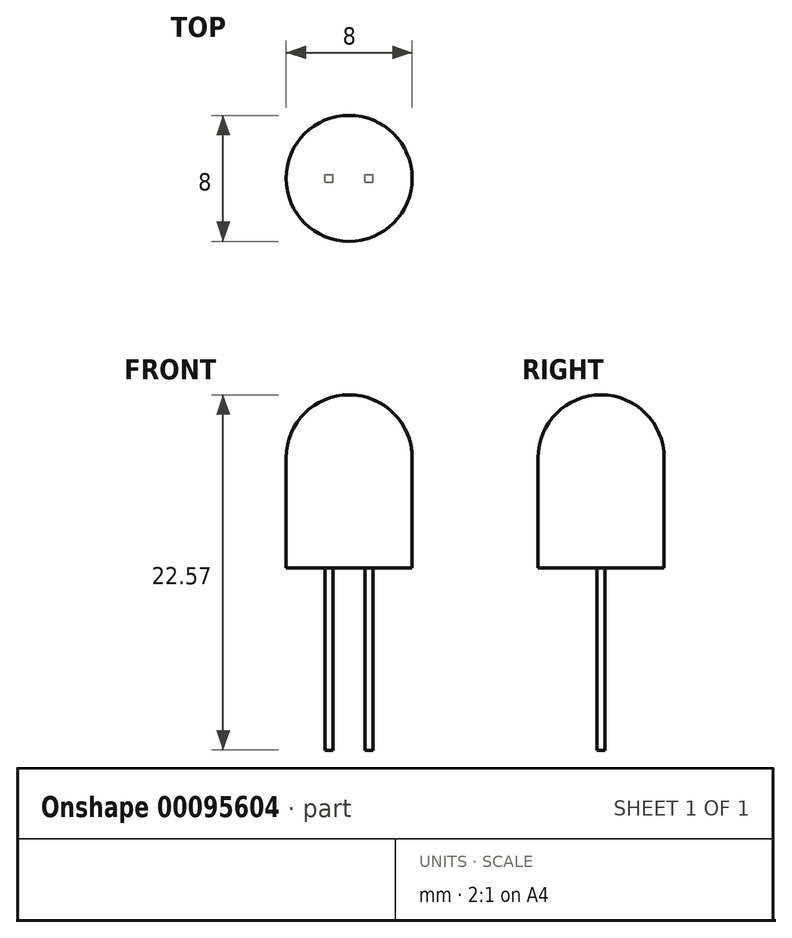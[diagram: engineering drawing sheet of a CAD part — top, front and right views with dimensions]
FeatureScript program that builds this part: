
annotation { "Feature Type Name" : "Feature", "Feature Type Description" : "" }
export const myFeature = defineFeature(function(context is Context, id is Id, definition is map)
    precondition{}
    {
        {
            var Q0;
            Q0=qCreatedBy(makeId("Front.planeOp"),FACE);
            var sketch = newSketch(context, id + "F0", { "sketchPlane" : qUnion([Q0])});
            skLineSegment(sketch, "E0", {"start": v(0, 0) * mm, "end": v(0, 11) * mm});
            skLineSegment(sketch, "E1", {"start": v(0, 0) * mm, "end": v(4, 0) * mm});
            skLineSegment(sketch, "E2", {"start": v(4, 0) * mm, "end": v(4, 7) * mm});
            skArc(sketch, "E3", {"start": v(4, 7) * mm, "mid": v(2.83, 9.83) * mm, "end": v(0, 11) * mm});
            skLineSegment(sketch, "E4", {"start": v(0, 0) * mm, "end": v(0, -3.6) * mm, "construction": true});
            skSolve(sketch);
        }
        {
            var Q0;
            Q0 = qSketchRegion(id + "F0", true);
            var Q1;
            Q1=sQuery(id+"F0.wireOp",EDGE,"E4");
            revolve(context, id + "F1", {"entities" : qUnion([Q0]), "axis" : qUnion([Q1]), "revolveType" : RevolveType.FULL});
        }
        {
            var Q0;
            Q0=qCreatedBy(makeId("Front.planeOp"),FACE);
            var sketch = newSketch(context, id + "F2", { "sketchPlane" : qUnion([Q0])});
            skLineSegment(sketch, "E5.bottom", {"start": v(1.02, 0) * mm, "end": v(1.52, 0) * mm});
            skLineSegment(sketch, "E5.top", {"start": v(1.02, -11.57) * mm, "end": v(1.52, -11.57) * mm});
            skLineSegment(sketch, "E5.left", {"start": v(1.02, 0) * mm, "end": v(1.02, -11.57) * mm});
            skLineSegment(sketch, "E5.right", {"start": v(1.52, 0) * mm, "end": v(1.52, -11.57) * mm});
            skLineSegment(sketch, "E6.bottom", {"start": v(-1.52, 0) * mm, "end": v(-1.02, 0) * mm});
            skLineSegment(sketch, "E6.top", {"start": v(-1.52, -11.57) * mm, "end": v(-1.02, -11.57) * mm});
            skLineSegment(sketch, "E6.left", {"start": v(-1.52, 0) * mm, "end": v(-1.52, -11.57) * mm});
            skLineSegment(sketch, "E6.right", {"start": v(-1.02, 0) * mm, "end": v(-1.02, -11.57) * mm});
            skLineSegment(sketch, "E7", {"start": v(0, 0) * mm, "end": v(0, -12) * mm, "construction": true});
            skSolve(sketch);
        }
        {
            var Q0;
            Q0 = qSketchRegion(id + "F2", true);
            extrude(context, id + "F3", {"entities" : qUnion([Q0]), "operationType" : NewBodyOperationType.ADD, "depth" : 0.5 * mm, "symmetric" : true});
        }
    });
